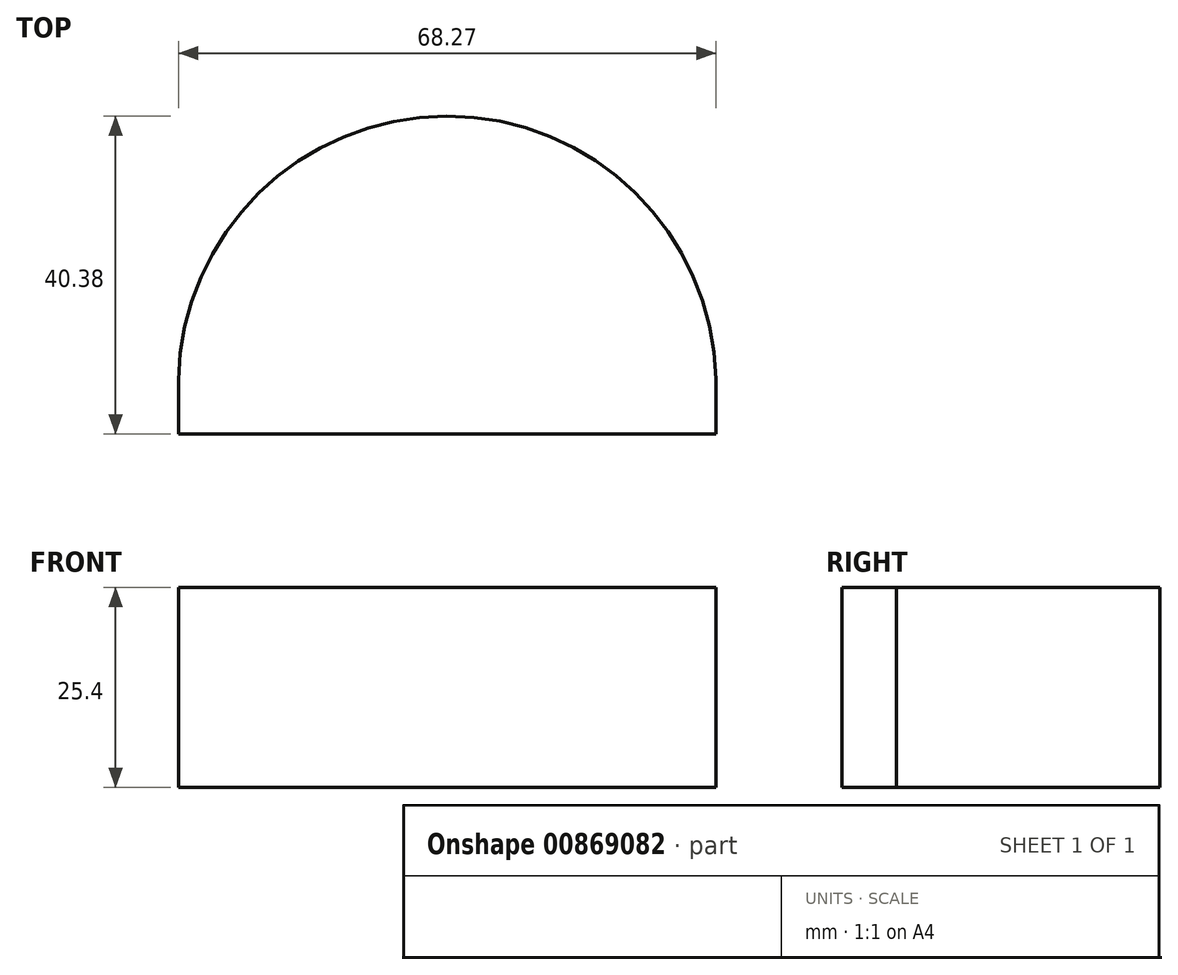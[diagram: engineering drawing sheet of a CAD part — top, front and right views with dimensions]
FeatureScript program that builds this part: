
annotation { "Feature Type Name" : "Feature", "Feature Type Description" : "" }
export const myFeature = defineFeature(function(context is Context, id is Id, definition is map)
    precondition{}
    {
        {
            var Q0;
            Q0=qCreatedBy(makeId("Top.planeOp"),FACE);
            var sketch = newSketch(context, id + "F0", { "sketchPlane" : qUnion([Q0])});
            skLineSegment(sketch, "E0.left", {"start": v(-34.07, -40.44) * mm, "end": v(-33.82, -197.66) * mm});
            skLineSegment(sketch, "E0.right", {"start": v(34.2, -40.34) * mm, "end": v(34.44, -197.56) * mm});
            skLineSegment(sketch, "E1", {"start": v(-33.82, -197.66) * mm, "end": v(34.44, -197.56) * mm});
            skArc(sketch, "E2", {"start": v(34.2, -40.34) * mm, "mid": v(0.01, -6.9) * mm, "end": v(-34.07, -40.44) * mm});
            skPoint(sketch, "E2.third.point", {"position": v(0, -6.9) * mm});
            skSolve(sketch);
        }
        {
            var Q0;
            Q0=makeQuery(id+"F0.imprint","IMPRINT",FACE,{"disambiguationData":[TD([[makeQuery(id+"F0.imprint","IMPRINT",EDGE,{"derivedFrom":sQuery(id+"F0.wireOp",EDGE,"nnsX8ZyO-u88p-AaUN-sSpN-ZOvoTn99LgBx")}),1.0]])]});
            var Q1;
            Q1=makeQuery(id+"F0.imprint","IMPRINT",FACE,{"disambiguationData":[TD([[makeQuery(id+"F0.imprint","IMPRINT",EDGE,{"derivedFrom":sQuery(id+"F0.wireOp",EDGE,"E0.left")}),1.0]])]});
            extrude(context, id + "F1", {"entities" : qUnion([Q0, Q1]), "depth" : 25.4 * mm, "offsetDistance" : 25.4 * mm});
        }
        {
            var Q0;
            Q0=makeQuery(id+"F1.opExtrude","CAP_FACE",FACE,{"disambiguationData":[OSD([sQuery(id+"F0.wireOp",EDGE,"nnsX8ZyO-u88p-AaUN-sSpN-ZOvoTn99LgBx"),sQuery(id+"F0.wireOp",EDGE,"E0.left"),sQuery(id+"F0.wireOp",EDGE,"E0.right"),sQuery(id+"F0.wireOp",EDGE,"WgsDUsan-A3dQ-eHmI-QTt8-hFEnIk3JPT0i"),sQuery(id+"F0.wireOp",EDGE,"mawbuG6N-awrq-46lC-s2GR-ikuSZYdzzbIp"),sQuery(id+"F0.wireOp",EDGE,"E1"),sQuery(id+"F0.wireOp",EDGE,"4608d917-8397-4fe6-9836-2379d33c07fc.filletArc"),sQuery(id+"F0.wireOp",EDGE,"fa2758ce-228f-42ff-8725-96282f76b5d2.filletArc")])],"isStart":true});
            var sketch = newSketch(context, id + "F2", { "sketchPlane" : qUnion([Q0])});
            skLineSegment(sketch, "E3.bottom", {"start": v(108.32, 47.3) * mm, "end": v(-125.47, 47.3) * mm});
            skLineSegment(sketch, "E3.top", {"start": v(108.32, 236.16) * mm, "end": v(-125.47, 236.16) * mm});
            skLineSegment(sketch, "E3.left", {"start": v(108.32, 47.3) * mm, "end": v(108.32, 236.16) * mm});
            skLineSegment(sketch, "E3.right", {"start": v(-125.47, 47.3) * mm, "end": v(-125.47, 236.16) * mm});
            skSolve(sketch);
        }
        {
            var Q0;
            Q0=qSketchRegion(id+"F2",true);
            extrude(context, id + "F3", {"entities" : qUnion([Q0]), "operationType" : NewBodyOperationType.REMOVE, "oppositeDirection" : true, "depth" : 91.95 * mm, "offsetDistance" : 25.4 * mm});
        }
    });
